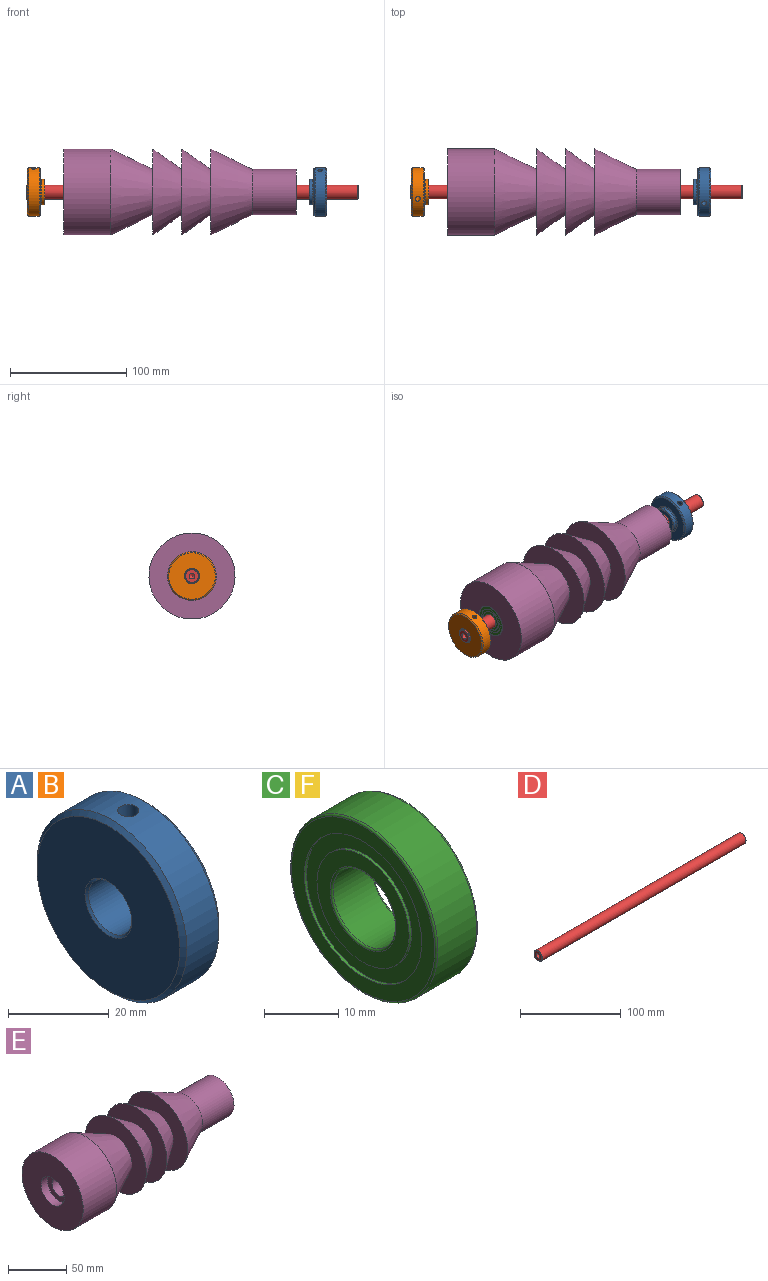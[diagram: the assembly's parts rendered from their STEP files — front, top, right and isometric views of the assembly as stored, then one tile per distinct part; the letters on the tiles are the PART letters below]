
ASSEMBLY  parts=6 mates=5
PART A: 13 faces, bbox 15x42x42 mm
  f0: cylinder r=21mm len=42mm, axis (-1,0,0), area 1173.6mm2, adj f7,f8,f11
  f1: cylinder r=6.05mm len=14mm, axis (1,0,0), area 518.1mm2, adj f9,f10,f11
  f2: plane 40x40mm, normal (1,0,0), area 804.2mm2, adj f6,f7
  f3: plane 40x40mm, normal (-1,0,0), area 1121.9mm2, adj f8,f9
  f4: cylinder r=11mm len=22mm, axis (-1,0,0), area 172.8mm2, adj f6,f12
  f5: plane 21x21mm, normal (1,0,0), area 211.6mm2, adj f10,f12
  f6: torus R=12mm, axis (1,0,0), area 112.2mm2, adj f2,f4
  f7: cone r=20mm half-angle=45deg, axis (-1,0,0), area 182.2mm2, adj f0,f2
  f8: cone r=21mm half-angle=45deg, axis (1,0,0), area 182.2mm2, adj f0,f3
  f9: cone r=6.05mm half-angle=45deg, axis (-1,0,0), area 28mm2, adj f1,f3
  f10: cone r=6.05mm half-angle=45deg, axis (1,0,0), area 28mm2, adj f1,f5
  f11: cylinder r=2.1mm len=15.33mm, axis (0,0,1), area 199mm2, adj f0,f1
  f12: cone r=10.5mm half-angle=45deg, axis (-1,0,0), area 47.8mm2, adj f4,f5
PART B: same geometry as A
PART C: 20 faces, bbox 8x30.3x30.3 mm
  f0: plane 17.6x17.6mm, normal (-1,0,0), area 118.6mm2, adj f1,f15
  f1: torus R=6.3mm, axis (1,0,0), area 18.1mm2, adj f0,f2
  f2: cylinder r=6mm len=12mm, axis (1,0,0), area 279mm2, adj f1,f3
  f3: torus R=6.3mm, axis (1,0,0), area 18.1mm2, adj f2,f4
  f4: plane 17.6x17.6mm, normal (1,0,0), area 118.6mm2, adj f3,f5
  f5: cylinder r=8.8mm len=17.6mm, axis (1,0,0), area 97.3mm2, adj f4,f6
  f6: plane 22.4x22.4mm, normal (1,0,0), area 150.8mm2, adj f5,f7
  f7: cylinder r=11.2mm len=22.4mm, axis (1,0,0), area 123.9mm2, adj f6,f8
  f8: plane 27.4x27.4mm, normal (1,0,0), area 195.6mm2, adj f7,f9
  f9: torus R=13.7mm, axis (1,0,0), area 41.1mm2, adj f8,f10
  f10: cylinder r=14mm len=28mm, axis (1,0,0), area 650.9mm2, adj f9,f11
  f11: torus R=13.7mm, axis (1,0,0), area 41.1mm2, adj f10,f12
  f12: plane 27.4x27.4mm, normal (-1,0,0), area 195.6mm2, adj f11,f13
  f13: cylinder r=11.2mm len=22.4mm, axis (1,0,0), area 30.3mm2, adj f12,f14
  f14: plane 22.4x22.4mm, normal (-1,0,0), area 150.8mm2, adj f13,f15
  f15: cylinder r=8.8mm len=17.6mm, axis (1,0,0), area 23.8mm2, adj f0,f14
  f16: plane 22.4x22.4mm, normal (1,0,0), area 150.8mm2, adj f17,f19
  f17: cylinder r=11.2mm len=22.4mm, axis (1,0,0), area 31mm2, adj f16,f18
  f18: plane 22.4x22.4mm, normal (-1,0,0), area 150.8mm2, adj f17,f19
  f19: cylinder r=8.8mm len=17.6mm, axis (1,0,0), area 24.3mm2, adj f16,f18
PART D: 9 faces, bbox 286x12x12 mm
  f0: cylinder r=6mm len=285mm, axis (-1,0,0), area 10744.2mm2, adj f7,f8
  f1: plane 11x11mm, normal (1,0,0), area 75.4mm2, adj f4,f8
  f2: plane 11x11mm, normal (-1,0,0), area 75.4mm2, adj f6,f7
  f3: cone r=0mm half-angle=59deg, axis (1,0,0), area 22.9mm2, adj f4
  f4: cylinder r=2.5mm len=20mm, axis (1,0,0), area 314.2mm2, adj f1,f3
  f5: cone r=0mm half-angle=59deg, axis (-1,0,0), area 22.9mm2, adj f6
  f6: cylinder r=2.5mm len=20mm, axis (-1,0,0), area 314.2mm2, adj f2,f5
  f7: cone r=6mm half-angle=45deg, axis (1,0,0), area 25.5mm2, adj f0,f2
  f8: cone r=5.5mm half-angle=45deg, axis (-1,0,0), area 25.5mm2, adj f0,f1
PART E: 16 faces, bbox 200.3x74.2x74.2 mm
  f0: cylinder r=14mm len=28mm, axis (-1,0,0), area 703.7mm2, adj f1,f15
  f1: plane 28x28mm, normal (-1,0,0), area 375.2mm2, adj f0,f2
  f2: cylinder r=8.75mm len=184.25mm, axis (-1,0,0), area 10129.7mm2, adj f1,f3
  f3: plane 28x28mm, normal (1,0,0), area 375.2mm2, adj f2,f4
  f4: cylinder r=14mm len=28mm, axis (-1,0,0), area 703.7mm2, adj f3,f5
  f5: plane 39x39mm, normal (1,0,0), area 578.8mm2, adj f4,f6
  f6: cylinder r=19.5mm len=39mm, axis (-1,0,0), area 4655.8mm2, adj f5,f7
  f7: cone r=37.07mm half-angle=26.2deg, axis (-1,0,0), area 7080.4mm2, adj f6,f8
  f8: plane 74.15x74.15mm, normal (-1,0,0), area 3123.7mm2, adj f7,f9
  f9: cone r=37.07mm half-angle=35.1deg, axis (-1,0,0), area 5431.5mm2, adj f8,f10
  f10: plane 74.15x74.15mm, normal (-1,0,0), area 3123.7mm2, adj f9,f11
  f11: cone r=37.07mm half-angle=35.1deg, axis (-1,0,0), area 5431.5mm2, adj f10,f12
  f12: plane 74.15x74.15mm, normal (-1,0,0), area 3123.7mm2, adj f11,f13
  f13: cone r=37.07mm half-angle=26deg, axis (-1,0,0), area 7120.3mm2, adj f12,f14
  f14: cylinder r=37.07mm len=74.15mm, axis (-1,0,0), area 9434.4mm2, adj f13,f15
  f15: plane 74.15x74.15mm, normal (-1,0,0), area 3702.5mm2, adj f0,f14
PART F: same geometry as C
PLACE A rot(axis=(0,-0.24,0.97),180deg) t=(125.99,-0.03,0.1)mm
PLACE B rot(axis=(1,0,0),16.5deg) t=(-131.71,-0.03,0.1)mm
PLACE C t=(-100.3,-0.03,0.1)mm
PLACE D rot(axis=(1,0,0),6.4deg) t=(10.01,-0.03,0.1)mm
PLACE E t=(-0.18,-0.03,0.1)mm fixed
PLACE F t=(91.95,-0.03,0.1)mm
MATE cylindrical C.f1 <-> E.f0  axis (1,0,0) through (-92.3,-0.03,0.1)mm
MATE cylindrical F.f1 <-> E.f0  axis (-1,0,0) through (91.95,-0.03,0.1)mm
MATE cylindrical A.f1 <-> F.f1  axis (-1,0,0) through (110.99,-0.03,0.1)mm
MATE cylindrical B.f1 <-> C.f1  axis (1,0,0) through (-116.71,-0.03,0.1)mm
MATE cylindrical D.f3 <-> F.f1  axis (1,0,0) through (153.01,-0.03,0.1)mm
